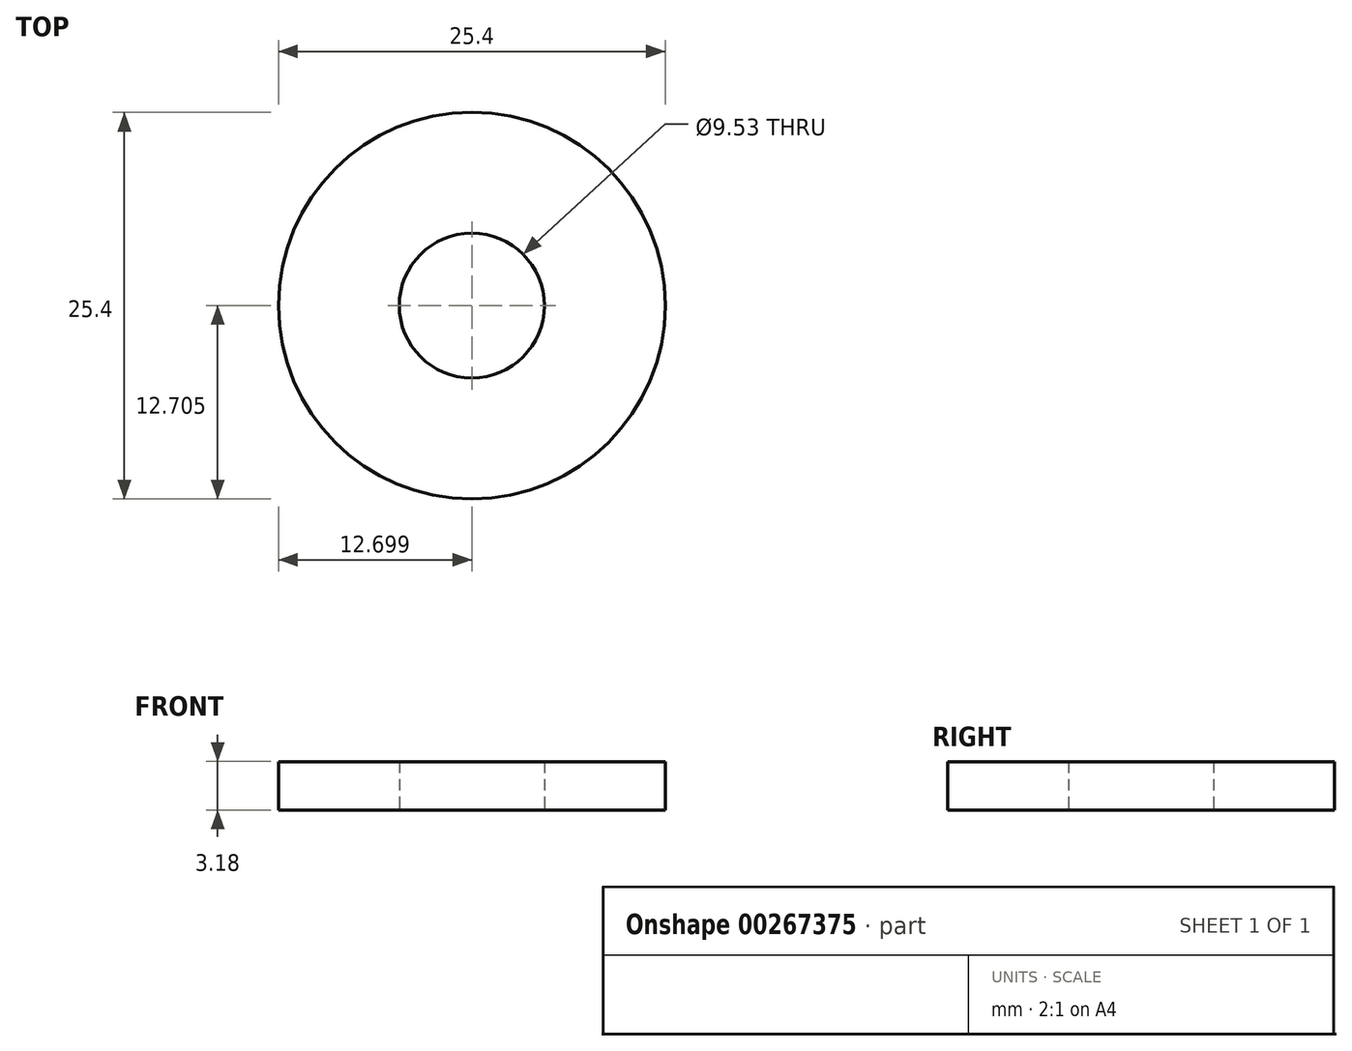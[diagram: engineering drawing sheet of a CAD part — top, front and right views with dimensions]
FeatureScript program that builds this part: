
annotation { "Feature Type Name" : "Feature", "Feature Type Description" : "" }
export const myFeature = defineFeature(function(context is Context, id is Id, definition is map)
    precondition{}
    {
        {
            var Q0;
            Q0=qCreatedBy(makeId("Top.planeOp"),FACE);
            var sketch = newSketch(context, id + "F0", { "sketchPlane" : qUnion([Q0])});
            skCircle(sketch, "E0", {"center": v(-24.36, -4) * mm, "radius": 12.7 * mm});
            skCircle(sketch, "E1", {"center": v(-24.36, -4) * mm, "radius": 4.76 * mm});
            skSolve(sketch);
        }
        {
            var Q0;
            Q0=makeQuery(id+"F0.imprint","IMPRINT",FACE,{"disambiguationData":[TD([[makeQuery(id+"F0.imprint","IMPRINT",EDGE,{"derivedFrom":sQuery(id+"F0.wireOp",EDGE,"E0")}),1.0]])]});
            extrude(context, id + "F1", {"entities" : qUnion([Q0]), "depth" : 3.17 * mm});
        }
    });
